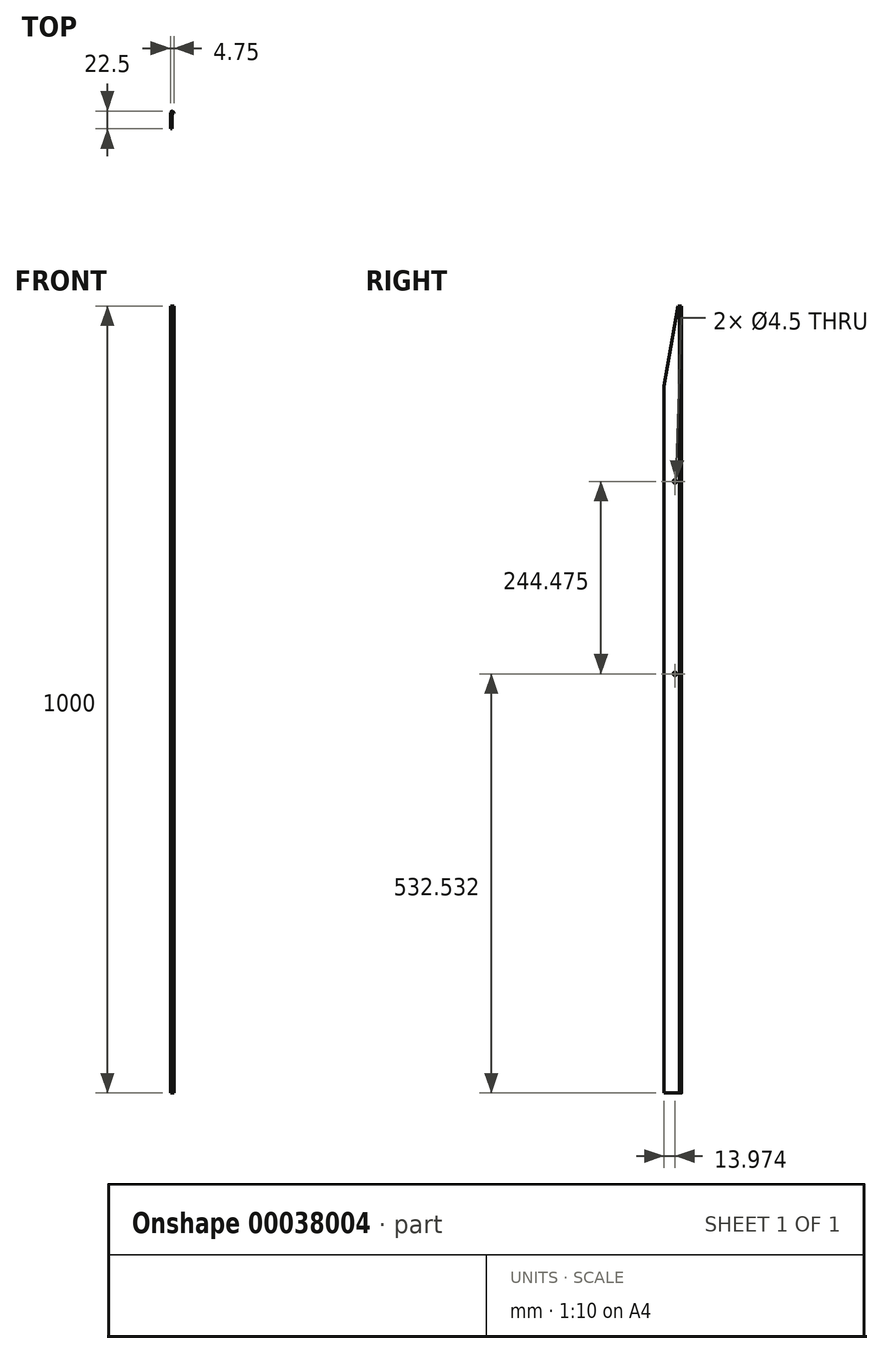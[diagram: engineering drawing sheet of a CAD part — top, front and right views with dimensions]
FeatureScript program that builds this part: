
annotation { "Feature Type Name" : "Feature", "Feature Type Description" : "" }
export const myFeature = defineFeature(function(context is Context, id is Id, definition is map)
    precondition{}
    {
        {
            var Q0;
            Q0=qCreatedBy(makeId("Top.planeOp"),FACE);
            var sketch = newSketch(context, id + "F0", { "sketchPlane" : qUnion([Q0])});
            skLineSegment(sketch, "E0.bottom", {"start": v(0, 0) * mm, "end": v(2.37, 0) * mm});
            skLineSegment(sketch, "E0.top", {"start": v(0, -19.53) * mm, "end": v(2.38, -19.53) * mm});
            skLineSegment(sketch, "E0.left", {"start": v(0, 0) * mm, "end": v(0, -19.53) * mm});
            skLineSegment(sketch, "E0.right", {"start": v(2.38, 0) * mm, "end": v(2.38, -19.53) * mm});
            skLineSegment(sketch, "E1", {"start": v(2.38, 0) * mm, "end": v(2.37, 2.97) * mm, "construction": true});
            skLineSegment(sketch, "E2", {"start": v(2.38, 0) * mm, "end": v(4.75, 0) * mm});
            skArc(sketch, "E3", {"start": v(2.94, 2.74) * mm, "mid": v(2.37, 2.97) * mm, "end": v(1.81, 2.74) * mm});
            skLineSegment(sketch, "E4", {"start": v(0, 0) * mm, "end": v(0, 0.92) * mm});
            skLineSegment(sketch, "E5", {"start": v(4.75, 0) * mm, "end": v(4.75, 0.92) * mm});
            skLineSegment(sketch, "E6", {"start": v(2.94, 2.74) * mm, "end": v(4.75, 0.92) * mm});
            skLineSegment(sketch, "E7", {"start": v(1.81, 2.74) * mm, "end": v(0, 0.92) * mm});
            skSolve(sketch);
        }
        {
            var Q0;
            Q0 = qSketchRegion(id + "F0", true);
            extrude(context, id + "F1", {"entities" : qUnion([Q0]), "depth" : 1000 * mm});
        }
        {
            var Q0;
            Q0=makeQuery(id+"F1.opExtrude","SWEPT_FACE",FACE,{"disambiguationData":[OSD([sQuery(id+"F0.wireOp",EDGE,"E0.left"),sQuery(id+"F0.wireOp",EDGE,"E4")])]});
            var sketch = newSketch(context, id + "F2", { "sketchPlane" : qUnion([Q0])});
            skLineSegment(sketch, "E8.bottom", {"start": v(19.53, 1000) * mm, "end": v(1.59, 1000) * mm});
            skLineSegment(sketch, "E8.top", {"start": v(19.53, 898.25) * mm, "end": v(1.59, 898.25) * mm, "construction": true});
            skLineSegment(sketch, "E8.left", {"start": v(19.53, 1000) * mm, "end": v(19.53, 898.25) * mm});
            skLineSegment(sketch, "E8.right", {"start": v(1.59, 1000) * mm, "end": v(1.59, 898.25) * mm, "construction": true});
            skLineSegment(sketch, "E9", {"start": v(1.59, 1000) * mm, "end": v(19.53, 898.25) * mm});
            skLineSegment(sketch, "E10", {"start": v(5.56, 898.25) * mm, "end": v(5.56, 777) * mm, "construction": true});
            skLineSegment(sketch, "E11", {"start": v(5.56, 777) * mm, "end": v(5.56, 532.53) * mm, "construction": true});
            skCircle(sketch, "E12", {"center": v(5.56, 777) * mm, "radius": 2.25 * mm});
            skCircle(sketch, "E13", {"center": v(5.56, 532.53) * mm, "radius": 2.25 * mm});
            skSolve(sketch);
        }
        {
            var Q0;
            Q0 = qSketchRegion(id + "F2", true);
            var Q1;
            Q1=makeQuery(id+"F1.opExtrude","SWEPT_FACE",FACE,{"disambiguationData":[OSD([sQuery(id+"F0.wireOp",EDGE,"E5")])]});
            extrude(context, id + "F3", {"entities" : qUnion([Q0]), "operationType" : NewBodyOperationType.REMOVE, "endBound" : BoundingType.UP_TO_SURFACE, "oppositeDirection" : true, "endBoundEntityFace" : qUnion([Q1]), "depth" : 25.4 * mm});
        }
    });
